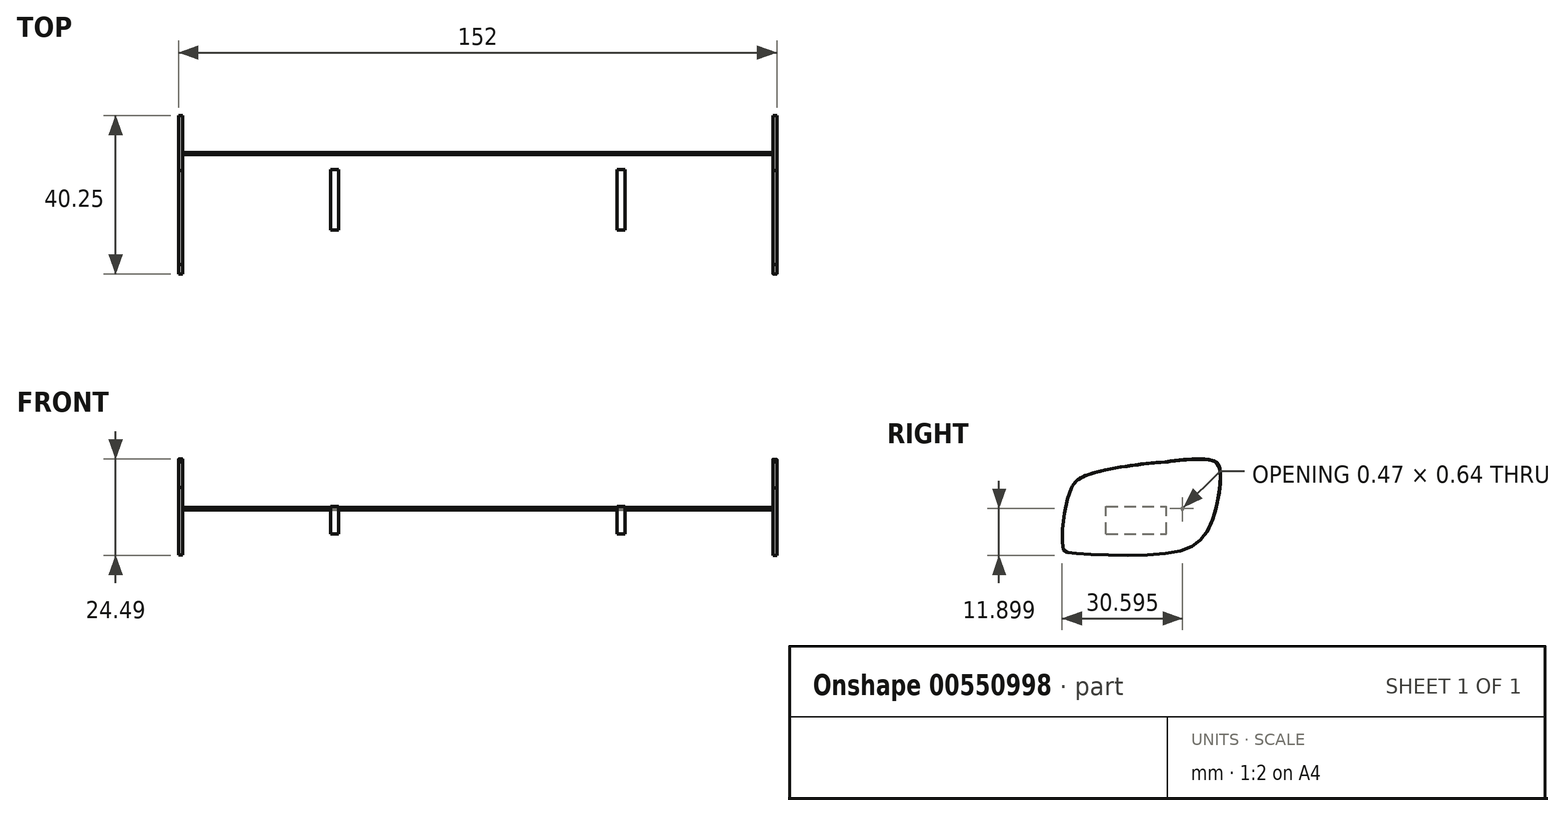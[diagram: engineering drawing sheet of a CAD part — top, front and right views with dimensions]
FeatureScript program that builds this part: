
annotation { "Feature Type Name" : "Feature", "Feature Type Description" : "" }
export const myFeature = defineFeature(function(context is Context, id is Id, definition is map)
    precondition{}
    {
        {
            var Q0;
            Q0=qCreatedBy(makeId("Right.planeOp"),FACE);
            var sketch = newSketch(context, id + "F0", { "sketchPlane" : qUnion([Q0])});
            skPoint(sketch, "E0", {"position": v(-107.77, 56.24) * mm});
            skPoint(sketch, "E1", {"position": v(49.68, 49.22) * mm});
            skPoint(sketch, "E2", {"position": v(39.35, 37.23) * mm});
            skPoint(sketch, "E3", {"position": v(96.38, -9.05) * mm});
            skPoint(sketch, "E4", {"position": v(96.38, -49.14) * mm});
            skPoint(sketch, "E5", {"position": v(115.4, -57.4) * mm});
            skPoint(sketch, "E6", {"position": v(115.4, -78.07) * mm});
            skLineSegment(sketch, "E7", {"start": v(48.4, 47.74) * mm, "end": v(39.35, 37.23) * mm});
            skPoint(sketch, "E8", {"position": v(45.35, 44.19) * mm});
            skFitSpline(sketch, "E9", {"points": [v(-107.77, 56.24) * mm, v(8.28, 52.26) * mm, v(49.68, 49.22) * mm], "startDerivative": vector(208.84, -5.82) * mm, "endDerivative": vector(96.65, -8.45) * mm});
            skFitSpline(sketch, "E10", {"points": [v(96.38, -49.14) * mm, v(112.64, -55.2) * mm, v(115.4, -57.4) * mm, v(115.4, -78.07) * mm], "startDerivative": vector(49.63, -18.32) * mm, "endDerivative": vector(-4.17, -61.24) * mm});
            skLineSegment(sketch, "E11", {"start": v(96.38, -16.6) * mm, "end": v(96.38, -47.74) * mm});
            skFitSpline(sketch, "E12", {"points": [v(31.4, 50.75) * mm, v(31.65, 44.28) * mm, v(39.35, 37.23) * mm, v(62.36, 11.1) * mm, v(73.42, -5.6) * mm, v(96.38, -9.05) * mm], "startDerivative": vector(-6.66, -55.67) * mm, "endDerivative": vector(115.26, 0.34) * mm});
            skFitSpline(sketch, "E13", {"points": [v(39.35, 37.23) * mm, v(60.49, 9.67) * mm, v(73.42, -5.6) * mm], "startDerivative": vector(39.23, -52.2) * mm, "endDerivative": vector(28.4, -32.57) * mm});
            skFitSpline(sketch, "E14", {"points": [v(60.49, 9.67) * mm, v(69.63, -1.81) * mm], "startDerivative": vector(9.14, -11.49) * mm, "endDerivative": vector(9.14, -11.49) * mm});
            skFitSpline(sketch, "E15", {"points": [v(91, -1.45) * mm, v(95.16, -8.53) * mm, v(96.38, -16.6) * mm], "startDerivative": vector(9.75, -13.63) * mm, "endDerivative": vector(1, -16.65) * mm});
            skArc(sketch, "E16.filletArc", {"start": v(96.38, -47.74) * mm, "mid": v(96.74, -48.89) * mm, "end": v(97.69, -49.62) * mm});
            skFitSpline(sketch, "E17", {"points": [v(44.52, 43.23) * mm, v(70.1, 22.19) * mm, v(91, -1.45) * mm], "startDerivative": vector(52.63, -39.98) * mm, "endDerivative": vector(40.3, -49.4) * mm});
            skArc(sketch, "E18.filletArc", {"start": v(48.4, 47.74) * mm, "mid": v(48.58, 48.77) * mm, "end": v(47.74, 49.39) * mm});
            skFitSpline(sketch, "E19", {"points": [v(96.38, -20.74) * mm, v(79.36, -20.94) * mm, v(72.54, -23.84) * mm, v(68.61, -35.2) * mm, v(67.79, -39.33) * mm, v(69.23, -41.4) * mm, v(96.38, -42.64) * mm], "startDerivative": vector(-87.15, 1.4) * mm, "endDerivative": vector(130.13, 2.89) * mm});
            skFitSpline(sketch, "E20", {"points": [v(83.7, -20.7) * mm, v(75.64, -24.04) * mm, v(68.61, -35.2) * mm], "startDerivative": vector(-19.14, -4.54) * mm, "endDerivative": vector(-11.3, -23.76) * mm});
            skLineSegment(sketch, "E21.top", {"start": v(55.1, 34.7) * mm, "end": v(55.6, 34.7) * mm});
            skPoint(sketch, "E22.visualSharp", {"position": v(88.1, 58.29) * mm});
            skPoint(sketch, "E23.visualSharp", {"position": v(53.1, 34.7) * mm});
            skArc(sketch, "E23.filletArc", {"start": v(53.1, 36.7) * mm, "mid": v(53.68, 35.28) * mm, "end": v(55.1, 34.7) * mm});
            skPoint(sketch, "E21.bottom.start.orphan", {"position": v(53.1, 58.29) * mm});
            skFitSpline(sketch, "E24.trimOffspring", {"points": [v(44.52, 43.23) * mm, v(70.1, 22.19) * mm, v(91, -1.45) * mm], "startDerivative": vector(52.63, -39.98) * mm, "endDerivative": vector(40.3, -49.4) * mm});
            skFitSpline(sketch, "E25", {"points": [v(63.86, 34.76) * mm, v(79.83, 20.28) * mm, v(95.32, 2.1) * mm, v(101.46, -9.95) * mm], "startDerivative": vector(44.88, -38.7) * mm, "endDerivative": vector(17.7, -41.42) * mm});
            skFitSpline(sketch, "E26", {"points": [v(99.82, -6.1) * mm, v(101.46, -9.95) * mm, v(97.8, -19.72) * mm, v(97.55, -22.07) * mm, v(97.69, -75.15) * mm], "startDerivative": vector(18.22, -20.9) * mm, "endDerivative": vector(-0.26, -138.73) * mm});
            skFitSpline(sketch, "E27", {"points": [v(78.5, 34.94) * mm, v(79.1, 29.37) * mm, v(103.2, 6.87) * mm, v(108.9, 1.17) * mm, v(111.09, -6.43) * mm, v(108.46, -17.39) * mm, v(111.67, -52.74) * mm, v(112.64, -75.98) * mm], "startDerivative": vector(-14.65, -54.98) * mm, "endDerivative": vector(-0.75, -120.7) * mm});
            skLineSegment(sketch, "E28.bottom", {"start": v(97.69, -75.15) * mm, "end": v(112.6, -75.15) * mm});
            skLineSegment(sketch, "E28.top", {"start": v(97.69, -66.48) * mm, "end": v(97.7, -66.48) * mm});
            skLineSegment(sketch, "E28.left", {"start": v(97.69, -75.15) * mm, "end": v(97.69, -66.48) * mm});
            skLineSegment(sketch, "E28.right", {"start": v(112.6, -75.15) * mm, "end": v(112.6, -66.48) * mm});
            skArc(sketch, "E29.filletArc", {"start": v(101.07, -11.93) * mm, "mid": v(101.26, -10.22) * mm, "end": v(100.86, -8.55) * mm});
            skFitSpline(sketch, "E30", {"points": [v(75.75, 32.94) * mm, v(75.75, 30.67) * mm, v(78.54, 26.85) * mm, v(84.94, 20.34) * mm, v(101.68, 5.67) * mm, v(104.36, 3.5) * mm, v(107.15, -0.12) * mm, v(108.4, -3.94) * mm], "startDerivative": vector(-4.6, -25.33) * mm, "endDerivative": vector(7.32, -33.09) * mm});
            skLineSegment(sketch, "E31", {"start": v(108.4, -3.94) * mm, "end": v(101.78, -3.94) * mm});
            skPoint(sketch, "E32.1.internal.orphan", {"position": v(100.54, -1.45) * mm});
            skFitSpline(sketch, "E33", {"points": [v(97.96, 1.85) * mm, v(99.5, -0.66) * mm, v(100.73, -3.22) * mm, v(100.93, -3.94) * mm], "startDerivative": vector(3.84, -5.9) * mm, "endDerivative": vector(0.63, -3) * mm});
            skLineSegment(sketch, "E34", {"start": v(101.78, -3.94) * mm, "end": v(100.93, -3.94) * mm});
            skCircle(sketch, "E35", {"center": v(102.89, -22.19) * mm, "radius": 3.64 * mm});
            skCircle(sketch, "E36", {"center": v(103.53, -33.17) * mm, "radius": 3.94 * mm});
            skCircle(sketch, "E37", {"center": v(104.18, -44.25) * mm, "radius": 4.69 * mm});
            skFitSpline(sketch, "E38", {"points": [v(69.12, 30.22) * mm, v(65.83, 34.76) * mm, v(64.8, 41.86) * mm], "startDerivative": vector(-8.2, 8.8) * mm, "endDerivative": vector(-0.61, 14.37) * mm});
            skFitSpline(sketch, "E39", {"points": [v(78.09, 33.38) * mm, v(78.5, 39) * mm, v(79.34, 41.73) * mm], "startDerivative": vector(0.33, 10.52) * mm, "endDerivative": vector(2.28, 5.92) * mm});
            skLineSegment(sketch, "E40", {"start": v(79.34, 41.73) * mm, "end": v(64.8, 41.86) * mm});
            skLineSegment(sketch, "E41", {"start": v(78.09, 33.38) * mm, "end": v(78.1, 32.54) * mm});
            skLineSegment(sketch, "E42", {"start": v(70.8, 28.71) * mm, "end": v(69.12, 30.22) * mm});
            skFitSpline(sketch, "E43", {"points": [v(72.05, 30.14) * mm, v(68.36, 33.3) * mm, v(67.11, 38.3) * mm, v(67.05, 39.94) * mm], "startDerivative": vector(-11.08, 6.69) * mm, "endDerivative": vector(-0.06, 6.14) * mm});
            skFitSpline(sketch, "E44", {"points": [v(75.75, 30.67) * mm, v(75.75, 34.1) * mm, v(76.38, 39.53) * mm], "startDerivative": vector(-0.25, 7.33) * mm, "endDerivative": vector(1.46, 10.28) * mm});
            skLineSegment(sketch, "E45", {"start": v(67.05, 39.94) * mm, "end": v(76.5, 39.86) * mm});
            skLineSegment(sketch, "E46", {"start": v(76.5, 39.86) * mm, "end": v(76.38, 39.53) * mm});
            skLineSegment(sketch, "E47", {"start": v(70.54, 31.1) * mm, "end": v(74.44, 27.9) * mm});
            skFitSpline(sketch, "E48.trimOffspring", {"points": [v(69.03, 32.94) * mm, v(89.18, 13.21) * mm, v(97.96, 1.85) * mm], "startDerivative": vector(38.44, -35.72) * mm, "endDerivative": vector(18.29, -25.93) * mm});
            skArc(sketch, "E49.filletArc", {"start": v(75.73, 31.02) * mm, "mid": v(75.8, 30.6) * mm, "end": v(75.93, 30.22) * mm});
            skCircle(sketch, "E50", {"center": v(104.89, -56.17) * mm, "radius": 4.69 * mm});
            skCircle(sketch, "E51", {"center": v(105.57, -67.89) * mm, "radius": 4.69 * mm});
            skArc(sketch, "E52", {"start": v(62.64, 51.93) * mm, "mid": v(59.56, 48.24) * mm, "end": v(63.17, 45.05) * mm});
            skFitSpline(sketch, "E53", {"points": [v(61.68, 51.69) * mm, v(71.34, 53.47) * mm, v(79.94, 53.6) * mm, v(80.88, 54.14) * mm, v(80.96, 56.08) * mm], "startDerivative": vector(24.85, 6.37) * mm, "endDerivative": vector(-0.92, 13.78) * mm});
            skFitSpline(sketch, "E54", {"points": [v(62.46, 45.09) * mm, v(72.41, 45.27) * mm, v(82.62, 48.9) * mm, v(83.83, 52.26) * mm, v(84.5, 54.9) * mm], "startDerivative": vector(31.08, -1.77) * mm, "endDerivative": vector(3.73, 23.57) * mm});
            skArc(sketch, "E55", {"start": v(83.5, 54.9) * mm, "mid": v(82.61, 55.78) * mm, "end": v(81.74, 54.88) * mm});
            skFitSpline(sketch, "E56", {"points": [v(79.94, 53.6) * mm, v(81.36, 54.22) * mm, v(81.8, 55.68) * mm, v(81.74, 54.88) * mm, v(81.74, 54.98) * mm], "startDerivative": vector(5.18, 1.29) * mm, "endDerivative": vector(0.08, 0.89) * mm});
            skFitSpline(sketch, "E57", {"points": [v(83.5, 54.9) * mm, v(83.36, 51.55) * mm, v(82.97, 49.7) * mm, v(82.62, 48.9) * mm], "startDerivative": vector(0, -12.07) * mm, "endDerivative": vector(-1.77, -3.67) * mm});
            skArc(sketch, "E58.filletArc", {"start": v(82.3, 48.58) * mm, "mid": v(82.57, 48.88) * mm, "end": v(82.78, 49.23) * mm});
            skFitSpline(sketch, "E59", {"points": [v(81.74, 54.96) * mm, v(81.73, 54.75) * mm, v(81.53, 54.22) * mm, v(80.8, 53.76) * mm, v(79.94, 53.6) * mm], "startDerivative": vector(-0.06, -1.23) * mm, "endDerivative": vector(-2.86, -0.31) * mm});
            skLineSegment(sketch, "E60", {"start": v(81.74, 54.98) * mm, "end": v(81.74, 54.96) * mm});
            skSolve(sketch);
        }
        {
            var Q0;
            {var subQ1=sQuery(id+"F0.wireOp",EDGE,"E57");Q0=makeQuery(id+"F0.imprint","IMPRINT",FACE,{"disambiguationData":[TD([[makeQuery(id+"F0.imprint","IMPRINT",EDGE,{"derivedFrom":subQ1}),-1.0]])]});}
            extrude(context, id + "F1", {"entities" : qUnion([Q0]), "depth" : 150 * mm, "offsetDistance" : 25 * mm, "symmetric" : true});
        }
        {
            var Q0;
            Q0=qCreatedBy(makeId("Top.planeOp"),FACE);
            cPlane(context, id + "F2", {"entities" : qUnion([Q0]), "cplaneType" : CPlaneType.OFFSET, "offset" : 49.4 * mm, "width" : 150 * mm, "height" : 150 * mm});
        }
        {
            var Q0;
            Q0=qCreatedBy(id+"F2.planeOp",FACE);
            var sketch = newSketch(context, id + "F3", { "sketchPlane" : qUnion([Q0])});
            skLineSegment(sketch, "E61.bottom", {"start": v(-37.41, 63.12) * mm, "end": v(-35.38, 63.12) * mm});
            skLineSegment(sketch, "E61.top", {"start": v(-37.41, 78.44) * mm, "end": v(-35.38, 78.44) * mm});
            skLineSegment(sketch, "E61.left", {"start": v(-37.41, 63.12) * mm, "end": v(-37.41, 78.44) * mm});
            skLineSegment(sketch, "E61.right", {"start": v(-35.38, 63.12) * mm, "end": v(-35.38, 78.44) * mm});
            skLineSegment(sketch, "E62.MirrorCS", {"start": v(37.41, 63.12) * mm, "end": v(37.41, 78.44) * mm});
            skLineSegment(sketch, "E63.MirrorCS", {"start": v(37.41, 63.12) * mm, "end": v(35.38, 63.12) * mm});
            skLineSegment(sketch, "E64.MirrorCS", {"start": v(35.38, 63.12) * mm, "end": v(35.38, 78.44) * mm});
            skLineSegment(sketch, "E65.MirrorCS", {"start": v(37.41, 78.44) * mm, "end": v(35.38, 78.44) * mm});
            skSolve(sketch);
        }
        {
            var Q0;
            Q0 = qSketchRegion(id + "F3", true);
            extrude(context, id + "F4", {"entities" : qUnion([Q0]), "operationType" : NewBodyOperationType.ADD, "oppositeDirection" : true, "depth" : 7 * mm, "offsetDistance" : 25 * mm});
        }
        {
            var Q0;
            Q0=makeQuery(id+"F1.opExtrude","CAP_FACE",FACE,{"disambiguationData":[OSD([sQuery(id+"F0.wireOp",EDGE,"E52"),sQuery(id+"F0.wireOp",EDGE,"E53"),sQuery(id+"F0.wireOp",EDGE,"E54"),sQuery(id+"F0.wireOp",EDGE,"E55"),sQuery(id+"F0.wireOp",EDGE,"E56"),sQuery(id+"F0.wireOp",EDGE,"E57"),sQuery(id+"F0.wireOp",EDGE,"E58.filletArc"),sQuery(id+"F0.wireOp",EDGE,"E59"),sQuery(id+"F0.wireOp",EDGE,"E60")])],"isStart":true});
            var sketch = newSketch(context, id + "F5", { "sketchPlane" : qUnion([Q0])});
            skFitSpline(sketch, "E66", {"points": [v(-89.56, 61.3) * mm, v(-74.73, 60.14) * mm, v(-58.74, 56.27) * mm, v(-54.37, 54.23) * mm, v(-52.14, 39.01) * mm, v(-54.08, 37.66) * mm, v(-79.57, 37.75) * mm, v(-89.36, 44.15) * mm, v(-91.98, 59.27) * mm, v(-89.56, 61.3) * mm]});
            skFitSpline(sketch, "E67", {"points": [v(-89.56, 61.3) * mm, v(-71.11, 60.08) * mm, v(-56.44, 56.58) * mm, v(-54.37, 54.23) * mm], "startDerivative": vector(41.6, -1.5) * mm, "endDerivative": vector(7.43, -13.67) * mm});
            skSolve(sketch);
        }
        {
            var Q0;
            Q0 = qSketchRegion(id + "F5", true);
            extrude(context, id + "F6", {"entities" : qUnion([Q0]), "operationType" : NewBodyOperationType.ADD, "depth" : 1 * mm, "offsetDistance" : 25 * mm});
        }
        {
            var Q0;
            Q0=makeQuery(id+"F1.opExtrude","CAP_FACE",FACE,{"disambiguationData":[OSD([sQuery(id+"F0.wireOp",EDGE,"E52"),sQuery(id+"F0.wireOp",EDGE,"E53"),sQuery(id+"F0.wireOp",EDGE,"E54"),sQuery(id+"F0.wireOp",EDGE,"E55"),sQuery(id+"F0.wireOp",EDGE,"E56"),sQuery(id+"F0.wireOp",EDGE,"E57"),sQuery(id+"F0.wireOp",EDGE,"E58.filletArc"),sQuery(id+"F0.wireOp",EDGE,"E59"),sQuery(id+"F0.wireOp",EDGE,"E60")])],"isStart":false});
            var sketch = newSketch(context, id + "F7", { "sketchPlane" : qUnion([Q0])});
            skFitSpline(sketch, "E68.MirrorCS", {"points": [v(89.51, 61.24) * mm, v(74.68, 60.08) * mm, v(58.7, 56.2) * mm, v(54.33, 54.17) * mm, v(52.1, 38.95) * mm, v(54.04, 37.6) * mm, v(79.53, 37.69) * mm, v(89.32, 44.09) * mm, v(91.94, 59.2) * mm, v(89.51, 61.24) * mm]});
            skFitSpline(sketch, "E69.MirrorCS", {"points": [v(89.51, 61.24) * mm, v(71.07, 60.02) * mm, v(56.4, 56.51) * mm, v(54.33, 54.17) * mm], "startDerivative": vector(-41.6, -1.5) * mm, "endDerivative": vector(-7.43, -13.67) * mm});
            skSolve(sketch);
        }
        {
            var Q0;
            Q0 = qSketchRegion(id + "F7", true);
            extrude(context, id + "F8", {"entities" : qUnion([Q0]), "operationType" : NewBodyOperationType.ADD, "depth" : 1 * mm, "offsetDistance" : 25 * mm});
        }
    });
